# Revit family: NLRS_63_LD_LUM-DL21LT-PGIN_luminaid
name_source: partatom
category: Lighting Devices
revit_build: Autodesk Revit 2018 (Build: 20190510_1515(x64)
units: mm (PartAtom-declared; Revit-internal decimal feet)

## family parameters
Always vertical = Yes
Cut with Voids When Loaded = No
Maintain Annotation Orientation = No
Part Type = Normal
Room Calculation Point = No
Round Connector Dimension = Use Diameter
Shared = No
Work Plane-Based = No

## types (5) — shared parameters
Diameter = 45 mm  [stored 0.147638 ft]
House = IP65
Impact Protection Rating = IK10
Manufacturer = LUMINAID B.V.
Product Brand = DATALUX.LT
Type = PLUG.IN

## per-type parameters (varying)
| type | 2 | 223 | 3 | Length | Passed signals |
| LUM-DL21LT-PGIN-D000 | No | No | No | 74 mm  [stored 0.242782 ft] | Luminaid SELV-DC power supply |
| LUM-DL21LT-PGIN-D00A | No | No | Yes | 75 mm | Luminaid SELV-DC power supply, AC power supply |
| LUM-DL21LT-PGIN-DE00 | Yes | No | No | 75 mm | Luminaid SELV-DC power supply, Emergency lighting (DCEM) |
| LUM-DL21LT-PGIN-DE0A | Yes | No | Yes | 75 mm | Luminaid SELV-DC power supply, Emergency lighting (DCEM), AC power supply |
| LUM-DL21LT-PGIN-DECA | Yes | Yes | Yes | 75 mm | Luminaid SELV-DC power supply, Emergency lighting (DCEM), Control 0-10V light control, AC power supply |

note: column(s) folded — value = type name in every type: Article code

type visibility flags: 5 boolean params named "<type name>" — each type sets only its own to Yes (folded from table)

note: [stored X ft] marks values corroborated as IEEE doubles in the binary element streams (Revit-internal decimal feet)

## geometry (parser evidence)
native form markers: Sweep x13
no freeform markers — native parametric forms only
